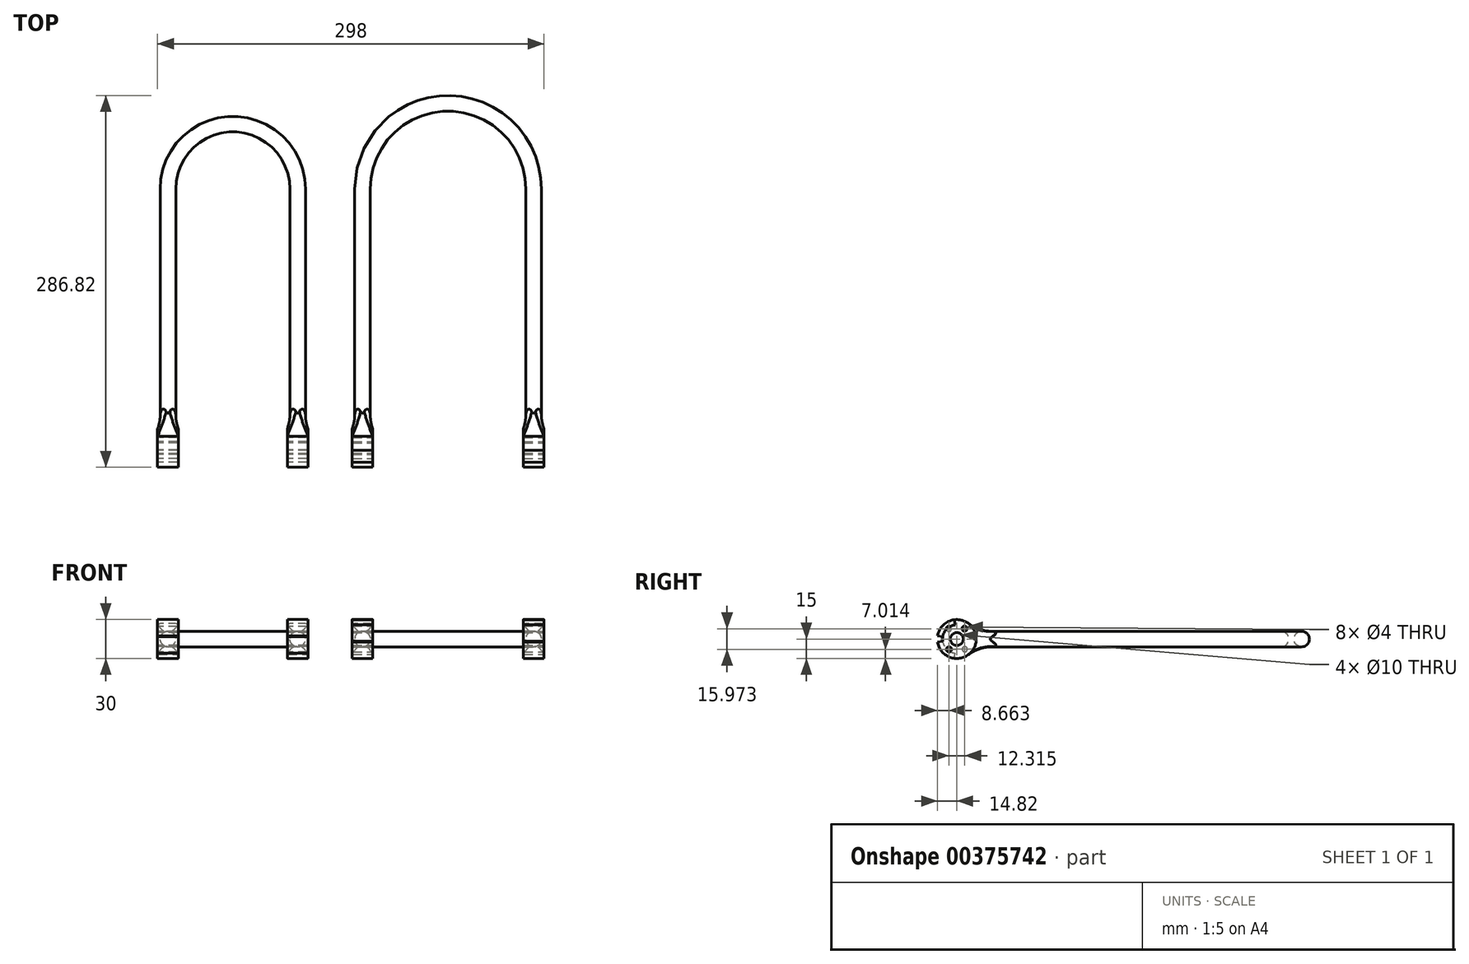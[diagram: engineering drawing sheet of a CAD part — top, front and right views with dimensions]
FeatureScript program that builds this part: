
annotation { "Feature Type Name" : "Feature", "Feature Type Description" : "" }
export const myFeature = defineFeature(function(context is Context, id is Id, definition is map)
    precondition{}
    {
        {
            var Q0;
            Q0=qCreatedBy(makeId("Front.planeOp"),FACE);
            var sketch = newSketch(context, id + "F0", { "sketchPlane" : qUnion([Q0])});
            skCircle(sketch, "E0", {"center": v(0, 0) * mm, "radius": 6 * mm});
            skSolve(sketch);
        }
        {
            var Q0;
            Q0=qCreatedBy(makeId("Top.planeOp"),FACE);
            var sketch = newSketch(context, id + "F1", { "sketchPlane" : qUnion([Q0])});
            skLineSegment(sketch, "E1", {"start": v(0, 0) * mm, "end": v(0, 200) * mm});
            skLineSegment(sketch, "E2", {"start": v(66, 266) * mm, "end": v(66, 266) * mm});
            skLineSegment(sketch, "E3", {"start": v(132, 200) * mm, "end": v(132, 0) * mm});
            skPoint(sketch, "E4.visualSharp", {"position": v(0, 266) * mm});
            skArc(sketch, "E4.filletArc", {"start": v(66, 266) * mm, "mid": v(19.33, 246.67) * mm, "end": v(0, 200) * mm});
            skPoint(sketch, "E5.visualSharp", {"position": v(132, 266) * mm});
            skArc(sketch, "E5.filletArc", {"start": v(132, 200) * mm, "mid": v(112.67, 246.67) * mm, "end": v(66, 266) * mm});
            skSolve(sketch);
        }
        {
            var Q0;
            Q0=makeQuery(id+"F0.imprint","IMPRINT",FACE,{"disambiguationData":[TD([[makeQuery(id+"F0.imprint","IMPRINT",EDGE,{"derivedFrom":sQuery(id+"F0.wireOp",EDGE,"E0")}),1.0]])]});
            var Q1;
            Q1=sQuery(id+"F1.wireOp",EDGE,"E1");
            var Q2;
            Q2=sQuery(id+"F1.wireOp",EDGE,"E4.filletArc");
            var Q3;
            Q3=sQuery(id+"F1.wireOp",EDGE,"E5.filletArc");
            var Q4;
            Q4=sQuery(id+"F1.wireOp",EDGE,"E3");
            sweep(context, id + "F2", {"profiles" : qUnion([Q0]), "path" : qUnion([Q1, Q2, Q3, Q4])});
        }
        {
            var Q0;
            Q0=qCreatedBy(makeId("Front.planeOp"),FACE);
            var sketch = newSketch(context, id + "F3", { "sketchPlane" : qUnion([Q0])});
            skCircle(sketch, "E6", {"center": v(-50, 0) * mm, "radius": 6 * mm});
            skSolve(sketch);
        }
        {
            var Q0;
            Q0=qCreatedBy(makeId("Top.planeOp"),FACE);
            var sketch = newSketch(context, id + "F4", { "sketchPlane" : qUnion([Q0])});
            skLineSegment(sketch, "E7", {"start": v(-50, 0) * mm, "end": v(-50, 200) * mm});
            skLineSegment(sketch, "E8", {"start": v(-100, 250) * mm, "end": v(-100, 250) * mm});
            skLineSegment(sketch, "E9", {"start": v(-150, 200) * mm, "end": v(-150, 0) * mm});
            skPoint(sketch, "E10.visualSharp", {"position": v(-150, 250) * mm});
            skArc(sketch, "E10.filletArc", {"start": v(-100, 250) * mm, "mid": v(-135.36, 235.36) * mm, "end": v(-150, 200) * mm});
            skPoint(sketch, "E11.visualSharp", {"position": v(-50, 250) * mm});
            skArc(sketch, "E11.filletArc", {"start": v(-50, 200) * mm, "mid": v(-64.64, 235.36) * mm, "end": v(-100, 250) * mm});
            skSolve(sketch);
        }
        {
            var Q0;
            Q0=makeQuery(id+"F3.imprint","IMPRINT",FACE,{"disambiguationData":[TD([[makeQuery(id+"F3.imprint","IMPRINT",EDGE,{"derivedFrom":sQuery(id+"F3.wireOp",EDGE,"E6")}),1.0]])]});
            var Q1;
            Q1=sQuery(id+"F4.wireOp",EDGE,"E7");
            var Q2;
            Q2=sQuery(id+"F4.wireOp",EDGE,"E9");
            var Q3;
            Q3=sQuery(id+"F4.wireOp",EDGE,"E11.filletArc");
            var Q4;
            Q4=sQuery(id+"F4.wireOp",EDGE,"E10.filletArc");
            sweep(context, id + "F5", {"profiles" : qUnion([Q0]), "path" : qUnion([Q1, Q2, Q3, Q4])});
        }
        {
            var Q0;
            Q0=qCreatedBy(makeId("Right.planeOp"),FACE);
            var sketch = newSketch(context, id + "F6", { "sketchPlane" : qUnion([Q0])});
            skCircle(sketch, "E12", {"center": v(0, 0) * mm, "radius": 15 * mm});
            skArc(sketch, "E13", {"start": v(0, -11) * mm, "mid": v(6.7, -8.73) * mm, "end": v(10.63, -2.85) * mm});
            skLineSegment(sketch, "E14", {"start": v(10.63, -2.85) * mm, "end": v(14.49, -3.88) * mm});
            skLineSegment(sketch, "E15", {"start": v(0, -11) * mm, "end": v(0, -15) * mm});
            skSolve(sketch);
        }
        {
            var Q0;
            Q0 = qSketchRegion(id + "F6", true);
            extrude(context, id + "F7", {"entities" : qUnion([Q0]), "operationType" : NewBodyOperationType.ADD, "depth" : 8 * mm});
        }
        {
            var Q0;
            Q0 = qSketchRegion(id + "F6", true);
            extrude(context, id + "F8", {"entities" : qUnion([Q0]), "operationType" : NewBodyOperationType.ADD, "oppositeDirection" : true, "depth" : 8 * mm});
        }
        {
            var Q0;
            Q0=makeQuery(id+"F8.boolean.opBoolean","INTERSECT",EDGE,{"disambiguationData":[OD(1.0)],"derivedFrom":[makeQuery(id+"F2.opSweep","SWEPT_FACE",FACE,{"disambiguationData":[OSD([sQuery(id+"F0.wireOp",EDGE,"E0"),sQuery(id+"F1.wireOp",EDGE,"E1")])]}),makeQuery(id+"F8.opExtrude","SWEPT_FACE",FACE,{"disambiguationData":[OSD([sQuery(id+"F6.wireOp",EDGE,"E12")])]})]});
            fillet(context, id + "F9", {"entities" : qUnion([Q0]), "radius" : 30 * mm, "tangentPropagation" : true, "allowEdgeOverflow" : false});
        }
        {
            var Q0;
            Q0=qCreatedBy(makeId("Right.planeOp"),FACE);
            cPlane(context, id + "F10", {"entities" : qUnion([Q0]), "cplaneType" : CPlaneType.OFFSET, "offset" : 132 * mm, "width" : 150 * mm, "height" : 150 * mm});
        }
        {
            var Q0;
            Q0=qCreatedBy(id+"F10.planeOp",FACE);
            var sketch = newSketch(context, id + "F11", { "sketchPlane" : qUnion([Q0])});
            skCircle(sketch, "E16", {"center": v(0, 0) * mm, "radius": 15 * mm});
            skSolve(sketch);
        }
        {
            var Q0;
            Q0=makeQuery(id+"F11.imprint","IMPRINT",FACE,{"disambiguationData":[TD([[makeQuery(id+"F11.imprint","IMPRINT",EDGE,{"derivedFrom":sQuery(id+"F11.wireOp",EDGE,"E16")}),1.0]])]});
            extrude(context, id + "F12", {"entities" : qUnion([Q0]), "operationType" : NewBodyOperationType.ADD, "depth" : 8 * mm});
        }
        {
            var Q0;
            Q0 = qSketchRegion(id + "F11", true);
            extrude(context, id + "F13", {"entities" : qUnion([Q0]), "operationType" : NewBodyOperationType.ADD, "oppositeDirection" : true, "depth" : 8 * mm});
        }
        {
            var Q0;
            Q0=makeQuery(id+"F13.boolean.opBoolean","INTERSECT",EDGE,{"disambiguationData":[OD(1.0)],"derivedFrom":[makeQuery(id+"F2.opSweep","SWEPT_FACE",FACE,{"disambiguationData":[OSD([sQuery(id+"F0.wireOp",EDGE,"E0"),sQuery(id+"F1.wireOp",EDGE,"E3")])]}),makeQuery(id+"F13.opExtrude","SWEPT_FACE",FACE,{"disambiguationData":[OSD([sQuery(id+"F11.wireOp",EDGE,"E16")])]})]});
            var Q1;
            Q1=makeQuery(id+"F13.boolean.opBoolean","INTERSECT",EDGE,{"disambiguationData":[OD(0.0)],"derivedFrom":[makeQuery(id+"F2.opSweep","SWEPT_FACE",FACE,{"disambiguationData":[OSD([sQuery(id+"F0.wireOp",EDGE,"E0"),sQuery(id+"F1.wireOp",EDGE,"E3")])]}),makeQuery(id+"F13.opExtrude","SWEPT_FACE",FACE,{"disambiguationData":[OSD([sQuery(id+"F11.wireOp",EDGE,"E16")])]})]});
            fillet(context, id + "F14", {"entities" : qUnion([Q0, Q1]), "radius" : 30 * mm, "tangentPropagation" : true, "allowEdgeOverflow" : false});
        }
        {
            var Q0;
            Q0=qCreatedBy(makeId("Right.planeOp"),FACE);
            cPlane(context, id + "F15", {"entities" : qUnion([Q0]), "cplaneType" : CPlaneType.OFFSET, "offset" : 50 * mm, "oppositeDirection" : true, "width" : 150 * mm, "height" : 150 * mm});
        }
        {
            var Q0;
            Q0=qCreatedBy(id+"F15.planeOp",FACE);
            var sketch = newSketch(context, id + "F16", { "sketchPlane" : qUnion([Q0])});
            skCircle(sketch, "E17", {"center": v(0, 0) * mm, "radius": 15 * mm});
            skSolve(sketch);
        }
        {
            var Q0;
            Q0 = qSketchRegion(id + "F16", true);
            extrude(context, id + "F17", {"entities" : qUnion([Q0]), "operationType" : NewBodyOperationType.ADD, "depth" : 8 * mm});
        }
        {
            var Q0;
            Q0 = qSketchRegion(id + "F16", true);
            extrude(context, id + "F18", {"entities" : qUnion([Q0]), "operationType" : NewBodyOperationType.ADD, "oppositeDirection" : true, "depth" : 8 * mm});
        }
        {
            var Q0;
            Q0=makeQuery(id+"F18.boolean.opBoolean","INTERSECT",EDGE,{"disambiguationData":[OD(1.0)],"derivedFrom":[makeQuery(id+"F5.opSweep","SWEPT_FACE",FACE,{"disambiguationData":[OSD([sQuery(id+"F3.wireOp",EDGE,"E6"),sQuery(id+"F4.wireOp",EDGE,"E7")])]}),makeQuery(id+"F18.opExtrude","SWEPT_FACE",FACE,{"disambiguationData":[OSD([sQuery(id+"F16.wireOp",EDGE,"E17")])]})]});
            var Q1;
            Q1=makeQuery(id+"F5.opSweep","SWEPT_FACE",FACE,{"disambiguationData":[OSD([sQuery(id+"F3.wireOp",EDGE,"E6"),sQuery(id+"F4.wireOp",EDGE,"E7")])]});
            fillet(context, id + "F19", {"entities" : qUnion([Q0, Q1]), "radius" : 30 * mm, "tangentPropagation" : true, "allowEdgeOverflow" : false});
        }
        {
            var Q0;
            Q0=qCreatedBy(id+"F15.planeOp",FACE);
            cPlane(context, id + "F20", {"entities" : qUnion([Q0]), "cplaneType" : CPlaneType.OFFSET, "offset" : 100 * mm, "oppositeDirection" : true, "width" : 150 * mm, "height" : 150 * mm});
        }
        {
            var Q0;
            Q0=qCreatedBy(id+"F20.planeOp",FACE);
            var sketch = newSketch(context, id + "F21", { "sketchPlane" : qUnion([Q0])});
            skCircle(sketch, "E18", {"center": v(0, 0) * mm, "radius": 15 * mm});
            skSolve(sketch);
        }
        {
            var Q0;
            Q0 = qSketchRegion(id + "F21", true);
            extrude(context, id + "F22", {"entities" : qUnion([Q0]), "operationType" : NewBodyOperationType.ADD, "depth" : 8 * mm});
        }
        {
            var Q0;
            Q0 = qSketchRegion(id + "F21", true);
            extrude(context, id + "F23", {"entities" : qUnion([Q0]), "operationType" : NewBodyOperationType.ADD, "oppositeDirection" : true, "depth" : 8 * mm});
        }
        {
            var Q0;
            Q0=makeQuery(id+"F23.boolean.opBoolean","INTERSECT",EDGE,{"disambiguationData":[OD(1.0)],"derivedFrom":[makeQuery(id+"F5.opSweep","SWEPT_FACE",FACE,{"disambiguationData":[OSD([sQuery(id+"F3.wireOp",EDGE,"E6"),sQuery(id+"F4.wireOp",EDGE,"E9")])]}),makeQuery(id+"F23.opExtrude","SWEPT_FACE",FACE,{"disambiguationData":[OSD([sQuery(id+"F21.wireOp",EDGE,"E18")])]})]});
            var Q1;
            Q1=makeQuery(id+"F23.boolean.opBoolean","INTERSECT",EDGE,{"disambiguationData":[OD(0.0)],"derivedFrom":[makeQuery(id+"F5.opSweep","SWEPT_FACE",FACE,{"disambiguationData":[OSD([sQuery(id+"F3.wireOp",EDGE,"E6"),sQuery(id+"F4.wireOp",EDGE,"E9")])]}),makeQuery(id+"F23.opExtrude","SWEPT_FACE",FACE,{"disambiguationData":[OSD([sQuery(id+"F21.wireOp",EDGE,"E18")])]})]});
            fillet(context, id + "F24", {"entities" : qUnion([Q0, Q1]), "radius" : 30 * mm, "tangentPropagation" : true, "allowEdgeOverflow" : false});
        }
        {
            var Q0;
            Q0=makeQuery(id+"F23.opExtrude","CAP_FACE",FACE,{"disambiguationData":[OSD([sQuery(id+"F21.wireOp",EDGE,"E18")])],"isStart":false});
            var sketch = newSketch(context, id + "F25", { "sketchPlane" : qUnion([Q0])});
            skCircle(sketch, "E19", {"center": v(0, 0) * mm, "radius": 5 * mm});
            skCircle(sketch, "E20", {"center": v(-6.16, -7.88) * mm, "radius": 2 * mm});
            skPoint(sketch, "E21.center.orphan", {"position": v(-10, 0) * mm});
            skPoint(sketch, "E22.center.orphan", {"position": v(10, 0) * mm});
            skLineSegment(sketch, "E23", {"start": v(0, 0) * mm, "end": v(5, 0) * mm});
            skCircle(sketch, "E24", {"center": v(6.16, 7.88) * mm, "radius": 2 * mm});
            skSolve(sketch);
        }
        {
            var Q0;
            Q0 = qSketchRegion(id + "F25", true);
            extrude(context, id + "F26", {"entities" : qUnion([Q0]), "operationType" : NewBodyOperationType.REMOVE, "oppositeDirection" : true, "depth" : 130 * mm});
        }
        {
            var Q0;
            Q0=makeQuery(id+"F12.opExtrude","CAP_FACE",FACE,{"disambiguationData":[OSD([sQuery(id+"F11.wireOp",EDGE,"E16")])],"isStart":false});
            var sketch = newSketch(context, id + "F27", { "sketchPlane" : qUnion([Q0])});
            skCircle(sketch, "E25", {"center": v(0, 0) * mm, "radius": 5 * mm});
            skSolve(sketch);
        }
        {
            var Q0;
            Q0 = qSketchRegion(id + "F27", true);
            extrude(context, id + "F28", {"entities" : qUnion([Q0]), "operationType" : NewBodyOperationType.REMOVE, "oppositeDirection" : true, "depth" : 180 * mm});
        }
        {
            var Q0;
            Q0=makeQuery(id+"F23.opExtrude","CAP_FACE",FACE,{"disambiguationData":[OSD([sQuery(id+"F21.wireOp",EDGE,"E18")])],"isStart":false});
            var sketch = newSketch(context, id + "F29", { "sketchPlane" : qUnion([Q0])});
            skLineSegment(sketch, "E26", {"start": v(10.86, 1.72) * mm, "end": v(14.82, 2.35) * mm});
            skLineSegment(sketch, "E27", {"start": v(1.34, -10.92) * mm, "end": v(1.83, -14.89) * mm});
            skPoint(sketch, "E28.end.orphan", {"position": v(15, 0) * mm});
            skArc(sketch, "E29", {"start": v(1.34, -10.92) * mm, "mid": v(8.78, -6.62) * mm, "end": v(10.86, 1.72) * mm});
            skSolve(sketch);
        }
        {
            var Q0;
            {var subQ0=sQuery(id+"F29.wireOp",EDGE,"E26");Q0=makeQuery(id+"F29.imprint","IMPRINT",FACE,{"disambiguationData":[TD([[makeQuery(id+"F29.imprint","IMPRINT",EDGE,{"derivedFrom":subQ0}),-1.0]])]});}
            extrude(context, id + "F30", {"entities" : qUnion([Q0]), "operationType" : NewBodyOperationType.REMOVE, "oppositeDirection" : true, "depth" : 150 * mm});
        }
        {
            var Q0;
            Q0=makeQuery(id+"F12.opExtrude","CAP_FACE",FACE,{"disambiguationData":[OSD([sQuery(id+"F11.wireOp",EDGE,"E16")])],"isStart":false});
            var sketch = newSketch(context, id + "F31", { "sketchPlane" : qUnion([Q0])});
            skLineSegment(sketch, "E30", {"start": v(-11, 0) * mm, "end": v(-15, 0) * mm});
            skLineSegment(sketch, "E31", {"start": v(0, 0) * mm, "end": v(-1.83, 14.89) * mm});
            skLineSegment(sketch, "E32", {"start": v(0, 0) * mm, "end": v(-14.82, -2.35) * mm});
            skArc(sketch, "E33", {"start": v(5.08, 9.75) * mm, "mid": v(-8.78, 6.62) * mm, "end": v(-7.98, -7.58) * mm});
            skLineSegment(sketch, "E34", {"start": v(0, 0) * mm, "end": v(4.81, 6.39) * mm});
            skCircle(sketch, "E35", {"center": v(6.02, 7.99) * mm, "radius": 2 * mm});
            skLineSegment(sketch, "E36.trimOffspring", {"start": v(7.22, 9.58) * mm, "end": v(9.03, 11.98) * mm});
            skCircle(sketch, "E37", {"center": v(-6.02, -7.99) * mm, "radius": 2 * mm});
            skLineSegment(sketch, "E38.trimOffspring", {"start": v(-4.81, -6.39) * mm, "end": v(0, 0) * mm});
            skSolve(sketch);
        }
        {
            var Q0;
            {var subQ0=sQuery(id+"F31.wireOp",EDGE,"E37");var subQ1=makeQuery(id+"F31.imprint","INTERSECT",VERTEX,{"derivedFrom":[sQuery(id+"F31.wireOp",EDGE,"E33"),subQ0]});Q0=makeQuery(id+"F31.imprint","IMPRINT",FACE,{"disambiguationData":[TD([[makeQuery(id+"F31.imprint","IMPRINT",EDGE,{"disambiguationData":[TD([[subQ1,1.0]])],"derivedFrom":subQ0}),1.0]])]});}
            var Q1;
            {var subQ0=sQuery(id+"F31.wireOp",EDGE,"E35");var subQ1=makeQuery(id+"F31.imprint","INTERSECT",VERTEX,{"derivedFrom":[sQuery(id+"F31.wireOp",EDGE,"E33"),subQ0]});Q1=makeQuery(id+"F31.imprint","IMPRINT",FACE,{"disambiguationData":[TD([[makeQuery(id+"F31.imprint","IMPRINT",EDGE,{"disambiguationData":[TD([[subQ1,1.0]])],"derivedFrom":subQ0}),1.0]])]});}
            var Q2;
            {var subQ0=sQuery(id+"F31.wireOp",EDGE,"E30");Q2=makeQuery(id+"F31.imprint","IMPRINT",FACE,{"disambiguationData":[TD([[makeQuery(id+"F31.imprint","IMPRINT",EDGE,{"derivedFrom":subQ0}),1.0]])]});}
            var Q3;
            {var subQ0=sQuery(id+"F31.wireOp",EDGE,"E30");Q3=makeQuery(id+"F31.imprint","IMPRINT",FACE,{"disambiguationData":[TD([[makeQuery(id+"F31.imprint","IMPRINT",EDGE,{"derivedFrom":subQ0}),-1.0]])]});}
            extrude(context, id + "F32", {"entities" : qUnion([Q0, Q1, Q2, Q3]), "operationType" : NewBodyOperationType.REMOVE, "oppositeDirection" : true, "depth" : 180 * mm});
        }
    });
